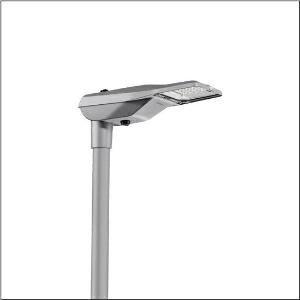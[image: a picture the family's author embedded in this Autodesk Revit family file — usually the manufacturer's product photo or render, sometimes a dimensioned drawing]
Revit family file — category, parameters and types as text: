
# Revit family: streetlight_sl_21_iq_micro___p0_8ab_5xe1r31y08cb_b23c
name_source: partatom
category: Lighting Fixtures
units: mm (PartAtom-declared; Revit-internal decimal feet)

## family parameters
Cut with Voids When Loaded = No
Host = Face
Light Source = No
Part Type = Normal
Room Calculation Point = No
Round Connector Dimension = Use Diameter
Shared = No

## types (1)
- --- (1 x LED, 2570 lm, 19.1 W, 3000K)
    Apparent Load = 19 VA
    CIE Flux Codes = 36 71 98 100 100
    Color Rendering = 70
    Color Temperature = 3000K
    Default Elevation = 1800 mm
    Description = Streetlight SL 21 iQ micro, mast luminaire, primary light control with lens, of PMMA, primary optical cover: cover, of toughened safety glass, transparent, light distribution: P0.8aB, light emission: direct distribution, primary light characteristic: asymmetric, installation type: post-top, side-entry, LED, High Power LED, rated luminous flux: 2.570lm, luminous efficacy: 135lm/W, light colour: 730, colour temperature: 3000K, control gear: iQ-Street Remote, D4i with power reduction, control: pre-setting: logarithmic dimming characteristic, Street-Remote, Auto-Match, Temp-Guard, Lumen-Switch, Night-Set, Smart-Wire, Light-Fading, Desk-Remote (wireless, voltage-free reading and setting of iQ features in the workshop via application-optimized NFC function/RFID function), optimised constant luminous flux control (CLO 2.0), mains connection: 220..240V, AC, 50/60Hz, start of lifetime: 19W, end of service life: 20W, reduction: 9W, luminaire housing, of diecast aluminium, powder-coated, Siteco® metallic grey (DB 702S), corrosivity category C5 high according to DIN EN ISO 12944, please order mast flange separately, inclination adjustable: 0°, 5°, 10°, 15°, sealing non-destructively replaceable, multi-level sealing system, length: 528mm, width: 235mm, height: 110mm, mast flange for spigot size: 42mm (side-entry): 5XC10008XM4, 60/48mm (side-entry/post-top): 5XC10108XM2, 76/60mm (side-entry/post-top): 5XC10108XM1, mounting height: 4..8m, Smart Interface below and above, protection rating (complete): IP66, insulation class (complete): insulation class II (safety insulation), certification: CE, ENEC, ENEC+, VDE, impact resistance: IK10, permissible operating ambient temperature for outdoor applications: -40..+50°C, standard-compliant lighting for roads and squares, packaging unit: 1 piece

Light Distribution: P0.8aB
    Height = 110 mm
    Lamp = 1 x LED
    Lamp Light Flux = 2570 lm
    Lamp Power = 19.1 W
    Lamp count = 1
    Length = 528 mm
    Luminous efficacy = 135 lm/W
    Manufacturer = Siteco
    ModVariant = No
    Model = 5XE1R31Y08CB
    Number of Poles = 1
    OnlyDefault = Yes
    Power Factor = 1
    Product Name = Streetlight SL 21 iQ micro | P0.8aB
    Product group = mast luminaire | pylon top
    ProductGroupID = 6100
    Protection Class = Protection class II
    Protection Degree = IP 66
    RLX_Detail_Level = 1
    RLX_Emergency_Light_Flux = 0 lm
    RLX_Emergency_Type = 0
    RLX_Emergency_Type_DB = No
    RlxData = <blob elided: 98285 chars, md5=f4459e3a>
    Socket = socket
    Standby Power = 0 W
    System Light Flux = 2570 lm
    System Power = 19 W
    Type Comments = factory setting: luminous flux: 100 % | dim-lin: 254 | 387 mA
    Type Image = l_1007239.jpg
    URL = http://relux.com
    VarID = @adj_086001
    Voltage = 0 V
    Weight = 0.00 kg
    Width = 235 mm

## geometry (parser evidence)
native form markers: Blend x4, Sweep x10
no freeform markers — native parametric forms only
